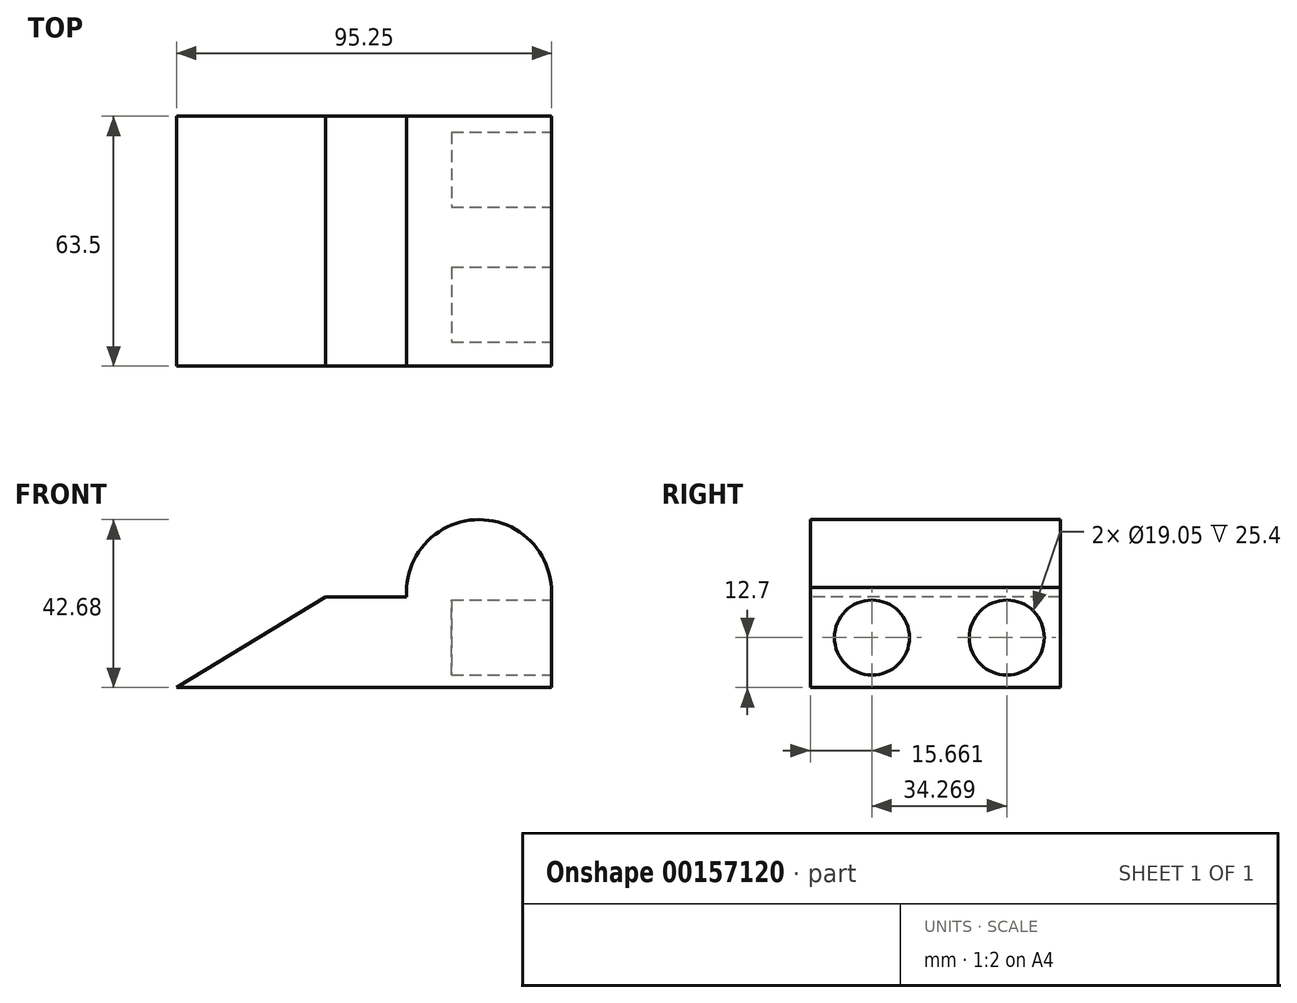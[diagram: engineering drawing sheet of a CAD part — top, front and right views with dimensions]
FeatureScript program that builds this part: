
annotation { "Feature Type Name" : "Feature", "Feature Type Description" : "" }
export const myFeature = defineFeature(function(context is Context, id is Id, definition is map)
    precondition{}
    {
        {
            var Q0;
            Q0=qCreatedBy(makeId("Top.planeOp"),FACE);
            var sketch = newSketch(context, id + "F0", { "sketchPlane" : qUnion([Q0])});
            skLineSegment(sketch, "E0.bottom", {"start": v(-77.07, -49.93) * mm, "end": v(18.18, -49.93) * mm});
            skLineSegment(sketch, "E0.top", {"start": v(-77.07, 13.57) * mm, "end": v(18.18, 13.57) * mm});
            skLineSegment(sketch, "E0.left", {"start": v(-77.07, -49.93) * mm, "end": v(-77.07, 13.57) * mm});
            skLineSegment(sketch, "E0.right", {"start": v(18.18, -49.93) * mm, "end": v(18.18, 13.57) * mm});
            skSolve(sketch);
        }
        {
            var Q0;
            Q0 = qSketchRegion(id + "F0", true);
            extrude(context, id + "F1", {"entities" : qUnion([Q0]), "depth" : 50.8 * mm});
        }
        {
            var Q0;
            Q0=makeQuery(id+"F1.opExtrude","SWEPT_FACE",FACE,{"disambiguationData":[OSD([sQuery(id+"F0.wireOp",EDGE,"E0.bottom")])]});
            var sketch = newSketch(context, id + "F2", { "sketchPlane" : qUnion([Q0])});
            skLineSegment(sketch, "E1", {"start": v(-77.07, 0) * mm, "end": v(-39.18, 23.1) * mm});
            skLineSegment(sketch, "E2", {"start": v(-39.18, 23.1) * mm, "end": v(-18.61, 23.1) * mm});
            skArc(sketch, "E3", {"start": v(18.18, 25.4) * mm, "mid": v(-1.37, 42.64) * mm, "end": v(-18.61, 23.1) * mm});
            skSolve(sketch);
        }
        {
            var Q0;
            Q0=makeQuery(id+"F2.imprint","IMPRINT",FACE,{"disambiguationData":[TD([[makeQuery(id+"F2.imprint","IMPRINT",EDGE,{"derivedFrom":sQuery(id+"F2.wireOp",EDGE,"E1")}),1.0]])]});
            extrude(context, id + "F3", {"entities" : qUnion([Q0]), "operationType" : NewBodyOperationType.REMOVE, "endBound" : BoundingType.THROUGH_ALL, "oppositeDirection" : true, "depth" : 25.4 * mm});
        }
        {
            var Q0;
            Q0=makeQuery(id+"F1.opExtrude","SWEPT_FACE",FACE,{"disambiguationData":[OSD([sQuery(id+"F0.wireOp",EDGE,"E0.right")])]});
            var sketch = newSketch(context, id + "F4", { "sketchPlane" : qUnion([Q0])});
            skLineSegment(sketch, "E4", {"start": v(-49.93, 12.7) * mm, "end": v(13.57, 12.7) * mm});
            skLineSegment(sketch, "E5", {"start": v(-18.18, 12.7) * mm, "end": v(-18.18, 0) * mm});
            skCircle(sketch, "E6", {"center": v(-34.27, 12.7) * mm, "radius": 9.53 * mm});
            skSolve(sketch);
        }
        {
            var Q0;
            Q0 = qSketchRegion(id + "F4", true);
            var Q1;
            {var subQ0=sQuery(id+"F4.wireOp",EDGE,"E6");var subQ1=sQuery(id+"F4.wireOp",EDGE,"E4");var subQ2=makeQuery(id+"F4.imprint","INTERSECT",VERTEX,{"disambiguationData":[OD(0.0)],"derivedFrom":[subQ1,subQ0]});Q1=makeQuery(id+"F4.imprint","IMPRINT",FACE,{"disambiguationData":[TD([[makeQuery(id+"F4.imprint","IMPRINT",EDGE,{"disambiguationData":[TD([[subQ2,-1.0]])],"derivedFrom":subQ1}),-1.0]])]});}
            extrude(context, id + "F5", {"entities" : qUnion([Q0, Q1]), "operationType" : NewBodyOperationType.REMOVE, "oppositeDirection" : true, "depth" : 25.4 * mm});
        }
        {
            var Q0;
            Q0=makeQuery(id+"F1.opExtrude","SWEPT_FACE",FACE,{"disambiguationData":[OSD([sQuery(id+"F0.wireOp",EDGE,"E0.right")])]});
            var sketch = newSketch(context, id + "F6", { "sketchPlane" : qUnion([Q0])});
            skLineSegment(sketch, "E7", {"start": v(13.57, 12.7) * mm, "end": v(-24.74, 12.7) * mm, "construction": true});
            skCircle(sketch, "E8", {"center": v(0, 12.7) * mm, "radius": 9.53 * mm});
            skSolve(sketch);
        }
        {
            var Q0;
            Q0=makeQuery(id+"F6.imprint","IMPRINT",FACE,{"disambiguationData":[TD([[makeQuery(id+"F6.imprint","IMPRINT",EDGE,{"derivedFrom":sQuery(id+"F6.wireOp",EDGE,"E8")}),1.0]])]});
            extrude(context, id + "F7", {"entities" : qUnion([Q0]), "operationType" : NewBodyOperationType.REMOVE, "oppositeDirection" : true, "depth" : 25.4 * mm});
        }
    });
